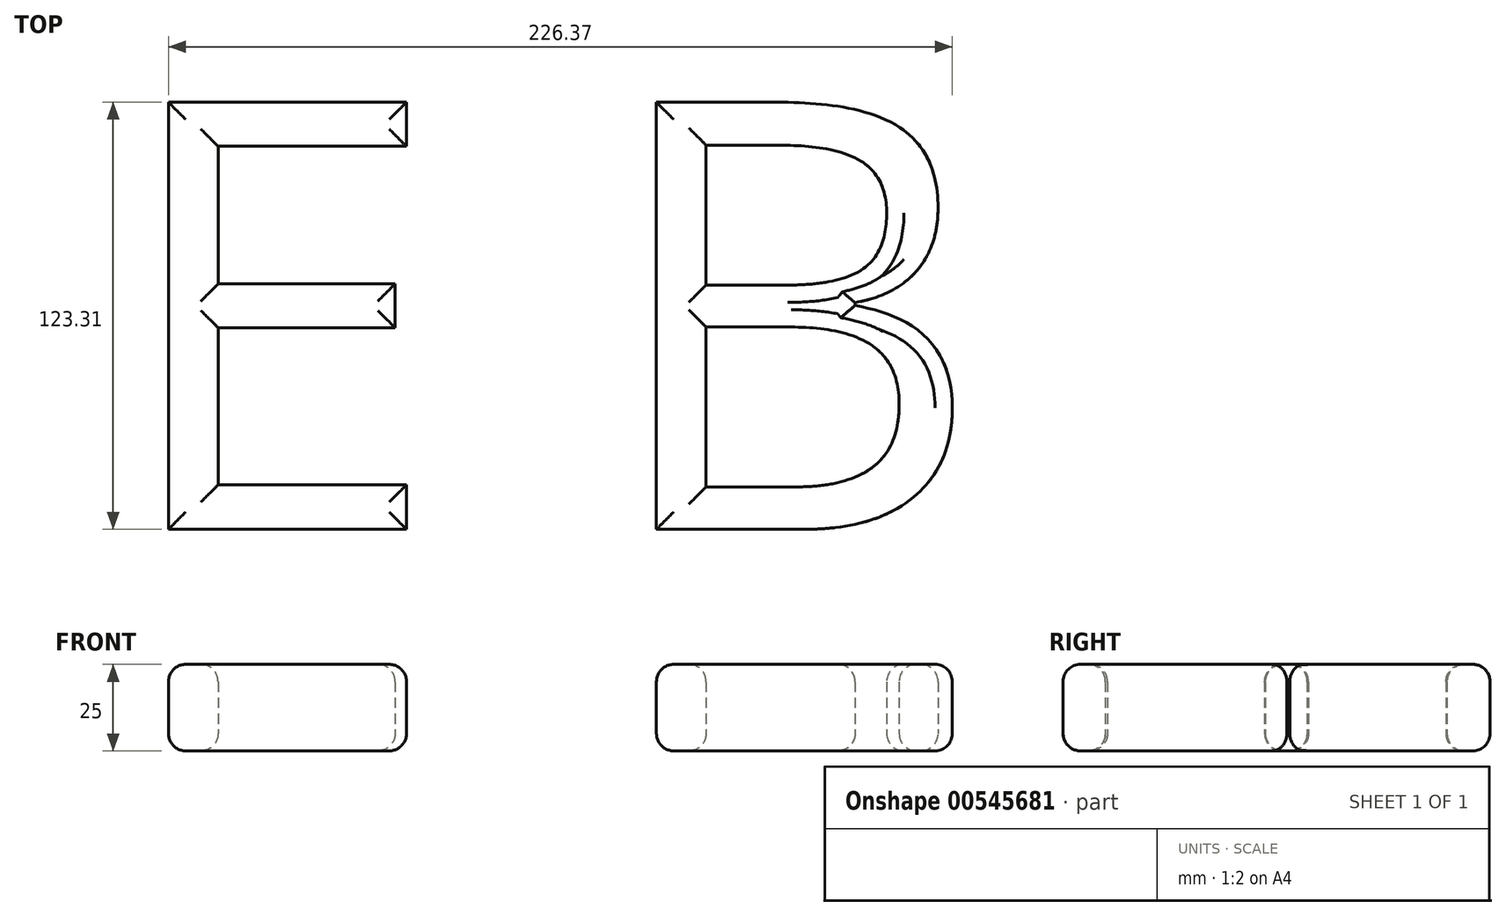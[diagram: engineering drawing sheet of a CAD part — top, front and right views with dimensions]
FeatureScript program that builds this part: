
annotation { "Feature Type Name" : "Feature", "Feature Type Description" : "" }
export const myFeature = defineFeature(function(context is Context, id is Id, definition is map)
    precondition{}
    {
        {
            var Q0;
            Q0=qCreatedBy(makeId("Top.planeOp"),FACE);
            var sketch = newSketch(context, id + "F0", { "sketchPlane" : qUnion([Q0])});
            skText(sketch, "E0", { "text": "E B", "fontName": "OpenSans-Regular.ttf"});
            const initialGuessF0  = {"E0": [-0.13682, -0.06572, 1, 0, 0.12436]};
            skSetInitialGuess(sketch, initialGuessF0);
            skSolve(sketch);
        }
        {
            var Q0;
            Q0=makeQuery(id+"F0.imprint","IMPRINT",FACE,{"disambiguationData":[TD([[makeQuery(id+"F0.imprint","IMPRINT",EDGE,{"derivedFrom":sQuery(id+"F0.wireOp",EDGE,"E0.sketch_text.stroke-0")}),-1.0]])]});
            var Q1;
            Q1=makeQuery(id+"F0.imprint","IMPRINT",FACE,{"disambiguationData":[TD([[makeQuery(id+"F0.imprint","IMPRINT",EDGE,{"derivedFrom":sQuery(id+"F0.wireOp",EDGE,"E0.sketch_text.stroke-12")}),-1.0]])]});
            extrude(context, id + "F1", {"entities" : qUnion([Q0, Q1]), "depth" : 25 * mm, "offsetDistance" : 25 * mm});
        }
        {
            var Q0;
            Q0=makeQuery(id+"F1.opExtrude","CAP_FACE",FACE,{"disambiguationData":[OSD([sQuery(id+"F0.wireOp",EDGE,"E0.sketch_text.stroke-12"),sQuery(id+"F0.wireOp",EDGE,"E0.sketch_text.stroke-13"),sQuery(id+"F0.wireOp",EDGE,"E0.sketch_text.stroke-14"),sQuery(id+"F0.wireOp",EDGE,"E0.sketch_text.stroke-15"),sQuery(id+"F0.wireOp",EDGE,"E0.sketch_text.stroke-16"),sQuery(id+"F0.wireOp",EDGE,"E0.sketch_text.stroke-17"),sQuery(id+"F0.wireOp",EDGE,"E0.sketch_text.stroke-18"),sQuery(id+"F0.wireOp",EDGE,"E0.sketch_text.stroke-19"),sQuery(id+"F0.wireOp",EDGE,"E0.sketch_text.stroke-20"),sQuery(id+"F0.wireOp",EDGE,"E0.sketch_text.stroke-21"),sQuery(id+"F0.wireOp",EDGE,"E0.sketch_text.stroke-22"),sQuery(id+"F0.wireOp",EDGE,"E0.sketch_text.stroke-23"),sQuery(id+"F0.wireOp",EDGE,"E0.sketch_text.stroke-24"),sQuery(id+"F0.wireOp",EDGE,"E0.sketch_text.stroke-25"),sQuery(id+"F0.wireOp",EDGE,"E0.sketch_text.stroke-26"),sQuery(id+"F0.wireOp",EDGE,"E0.sketch_text.stroke-27"),sQuery(id+"F0.wireOp",EDGE,"E0.sketch_text.stroke-28"),sQuery(id+"F0.wireOp",EDGE,"E0.sketch_text.stroke-29"),sQuery(id+"F0.wireOp",EDGE,"E0.sketch_text.stroke-30"),sQuery(id+"F0.wireOp",EDGE,"E0.sketch_text.stroke-31"),sQuery(id+"F0.wireOp",EDGE,"E0.sketch_text.stroke-32"),sQuery(id+"F0.wireOp",EDGE,"E0.sketch_text.stroke-33"),sQuery(id+"F0.wireOp",EDGE,"E0.sketch_text.stroke-34"),sQuery(id+"F0.wireOp",EDGE,"E0.sketch_text.stroke-35"),sQuery(id+"F0.wireOp",EDGE,"E0.sketch_text.stroke-36")])],"isStart":false});
            fillet(context, id + "F2", {"entities" : qUnion([Q0]), "radius" : 5 * mm, "tangentPropagation" : true, "allowEdgeOverflow" : false});
        }
        {
            var Q0;
            Q0=makeQuery(id+"F1.opExtrude","CAP_FACE",FACE,{"disambiguationData":[OSD([sQuery(id+"F0.wireOp",EDGE,"E0.sketch_text.stroke-0"),sQuery(id+"F0.wireOp",EDGE,"E0.sketch_text.stroke-1"),sQuery(id+"F0.wireOp",EDGE,"E0.sketch_text.stroke-2"),sQuery(id+"F0.wireOp",EDGE,"E0.sketch_text.stroke-3"),sQuery(id+"F0.wireOp",EDGE,"E0.sketch_text.stroke-4"),sQuery(id+"F0.wireOp",EDGE,"E0.sketch_text.stroke-5"),sQuery(id+"F0.wireOp",EDGE,"E0.sketch_text.stroke-6"),sQuery(id+"F0.wireOp",EDGE,"E0.sketch_text.stroke-7"),sQuery(id+"F0.wireOp",EDGE,"E0.sketch_text.stroke-8"),sQuery(id+"F0.wireOp",EDGE,"E0.sketch_text.stroke-9"),sQuery(id+"F0.wireOp",EDGE,"E0.sketch_text.stroke-10"),sQuery(id+"F0.wireOp",EDGE,"E0.sketch_text.stroke-11")])],"isStart":false});
            fillet(context, id + "F3", {"entities" : qUnion([Q0]), "radius" : 5 * mm, "tangentPropagation" : true, "allowEdgeOverflow" : false});
        }
        {
            var Q0;
            Q0=makeQuery(id+"F1.opExtrude","CAP_FACE",FACE,{"disambiguationData":[OSD([sQuery(id+"F0.wireOp",EDGE,"E0.sketch_text.stroke-0"),sQuery(id+"F0.wireOp",EDGE,"E0.sketch_text.stroke-1"),sQuery(id+"F0.wireOp",EDGE,"E0.sketch_text.stroke-2"),sQuery(id+"F0.wireOp",EDGE,"E0.sketch_text.stroke-3"),sQuery(id+"F0.wireOp",EDGE,"E0.sketch_text.stroke-4"),sQuery(id+"F0.wireOp",EDGE,"E0.sketch_text.stroke-5"),sQuery(id+"F0.wireOp",EDGE,"E0.sketch_text.stroke-6"),sQuery(id+"F0.wireOp",EDGE,"E0.sketch_text.stroke-7"),sQuery(id+"F0.wireOp",EDGE,"E0.sketch_text.stroke-8"),sQuery(id+"F0.wireOp",EDGE,"E0.sketch_text.stroke-9"),sQuery(id+"F0.wireOp",EDGE,"E0.sketch_text.stroke-10"),sQuery(id+"F0.wireOp",EDGE,"E0.sketch_text.stroke-11")])],"isStart":true});
            var Q1;
            Q1=makeQuery(id+"F1.opExtrude","CAP_FACE",FACE,{"disambiguationData":[OSD([sQuery(id+"F0.wireOp",EDGE,"E0.sketch_text.stroke-12"),sQuery(id+"F0.wireOp",EDGE,"E0.sketch_text.stroke-13"),sQuery(id+"F0.wireOp",EDGE,"E0.sketch_text.stroke-14"),sQuery(id+"F0.wireOp",EDGE,"E0.sketch_text.stroke-15"),sQuery(id+"F0.wireOp",EDGE,"E0.sketch_text.stroke-16"),sQuery(id+"F0.wireOp",EDGE,"E0.sketch_text.stroke-17"),sQuery(id+"F0.wireOp",EDGE,"E0.sketch_text.stroke-18"),sQuery(id+"F0.wireOp",EDGE,"E0.sketch_text.stroke-19"),sQuery(id+"F0.wireOp",EDGE,"E0.sketch_text.stroke-20"),sQuery(id+"F0.wireOp",EDGE,"E0.sketch_text.stroke-21"),sQuery(id+"F0.wireOp",EDGE,"E0.sketch_text.stroke-22"),sQuery(id+"F0.wireOp",EDGE,"E0.sketch_text.stroke-23"),sQuery(id+"F0.wireOp",EDGE,"E0.sketch_text.stroke-24"),sQuery(id+"F0.wireOp",EDGE,"E0.sketch_text.stroke-25"),sQuery(id+"F0.wireOp",EDGE,"E0.sketch_text.stroke-26"),sQuery(id+"F0.wireOp",EDGE,"E0.sketch_text.stroke-27"),sQuery(id+"F0.wireOp",EDGE,"E0.sketch_text.stroke-28"),sQuery(id+"F0.wireOp",EDGE,"E0.sketch_text.stroke-29"),sQuery(id+"F0.wireOp",EDGE,"E0.sketch_text.stroke-30"),sQuery(id+"F0.wireOp",EDGE,"E0.sketch_text.stroke-31"),sQuery(id+"F0.wireOp",EDGE,"E0.sketch_text.stroke-32"),sQuery(id+"F0.wireOp",EDGE,"E0.sketch_text.stroke-33"),sQuery(id+"F0.wireOp",EDGE,"E0.sketch_text.stroke-34"),sQuery(id+"F0.wireOp",EDGE,"E0.sketch_text.stroke-35"),sQuery(id+"F0.wireOp",EDGE,"E0.sketch_text.stroke-36")])],"isStart":true});
            fillet(context, id + "F4", {"entities" : qUnion([Q0, Q1]), "radius" : 5 * mm, "tangentPropagation" : true, "allowEdgeOverflow" : false});
        }
    });
